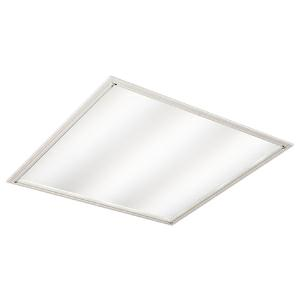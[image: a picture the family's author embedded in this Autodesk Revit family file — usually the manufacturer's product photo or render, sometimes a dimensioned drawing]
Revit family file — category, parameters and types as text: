
# Revit family: 3f_filippi_-_l_320_lgs_3f_filippi_-_21581_-_l_324x10w_led_lgs_596x596
name_source: partatom
category: Lighting Fixtures
units: mm (PartAtom-declared; Revit-internal decimal feet)

## family parameters
Cut with Voids When Loaded = No
Host = Face
Light Source = No
Part Type = Normal
Room Calculation Point = No
Round Connector Dimension = Use Diameter
Shared = No

## types (1)
- 3F Filippi - L 320 LGS (1 x LED, 4292 lm, 45 W, 4000 K)
    Apparent Load = 45 VA
    Approval mark = ENEC
    CIE Flux Codes = 62 88 97 100 100
    Color Rendering = 80
    Color Temperature = 4000 K
    Control Gear = Electronic ballast
    Default Elevation = 1800 mm
    Description = ILLUMINOTECHNICAL
Luminous efficiency 100% (DLOR 100%, ULOR 0%).
Initial luminous flux of the luminaire 4292 lm.
Direct symmetric distribution.
Installation Interdistance Transv.D = 1.16 x hu - Long.D = 1.16 x hu.
Average luminance <3000 cd/m² for radial angles >65°.
Tabular UGR (CIE 117 - 4H-8H; S=0.25H; 70/50/20): RUG 18.8 - 18.8.
Beam angle: 85° - 84°.
Luminous efficacy 95 lm/W.
Lifetime (L93/B10): 30000 h. (tq+25°C)
Lifetime (L90/B10): 50000 h. (tq+25°C)
Lifetime (L85/B10): 80000 h. (tq+25°C)
Lifetime (L80/B10): 100000 h. (tq+25°C)
Sudden decreased luminous flux after 50000 hours: 0% (C0).
Photobiological safety in compliance with IEC/TR 62778: RG0 risk exempt, (IEC 62471).
In compliance with IEC/EN 62722-2-1 - IEC/EN 62717 standards.

SOURCE
4 linear LED modules 10W/840.
Energy efficiency class (UE 2019/2020 - UE 2019/2015): D.
CIE 13.3 Colour rendering index: CRI >80 (R9 <50%).
IES TM-30 Fidelity Index: Rf = 84 Rg = 95.
CCT nominal colour temperature 4000 K.
Colour initial tolerance (MacAdam): SDCM 2.

MECHANICAL
Housing in hot-galvanised steel, painted in white polyester.
Micro-prismatic flat diffuser in transparent methacrylate (PMMA), multilenticular exterior, anti-glare, locked to the white painted aluminium perimetral frame, sealing gasket, hinged opening.
Anti-glare opal polycarbonate filter for brightness uniformity.
Luminaire with limited surface temperature. - D - (EN 60598-2-24)
Dimensions: 596x596 mm, height 80 mm. Weight 4.715 kg.
IP54 protection degree for exposed part, IP20 for recessed part.
Mechanical strength to impacts IK06 (1 joule).
Glow-wire test resistance 650°C.

ELECTRICAL
Halogen Free electronic wiring 230V-50/60Hz, power factor 0.95, THD <25%, constant output current, SELV, class I, 1 driver.
Power of the luminaire 45 W.
CE - IEC 60598-1 - EN 60598-1.
SAFE FLICKER: PstLM=<1 and SVM=<0.4 (IEC TR 61547-1 and IEC TR 63158), to ensure a more comfortable and safe light.
Luminaire compliant with EN 60598-2-22 for power supply from a centralised emergency system CPSS (Central Power Supply System), not incorporated in the luminaire - high risk areas excluded. The default power and flux are 100% in AC and 100% in DC.
Ambient temperature from 0°C to +25°C.
Temperature class T6 max 85°C.
Relative humidity UR: <85%.

INSTALLATION
Lay-in recessed fitting.
On request: pull-up recessed fitting with brackets.
False ceiling carving: 580x580 mm.
All accessories dedicated to this product are available on the Catalog and on our website www.3F-Filippi.com.

APPLICATIONS
Environments: sterilized, aseptic.
In environments with VDU's, managerial offices and staterooms, environments involving accurate visual tasks where a diffused and soft light for an optimum visual comfort and the source total shielding are required.

WARNING
Luminaire designed for disposal/recycling at end-of-life.
Replaceable (LED only) light source by a professional. Replaceable control gear by a professional.
    Height = 0 mm  [stored 0 ft]
    Lamp = 1 x LED
    Lamp Light Flux = 4292 lm
    Lamp Power = 45 W
    Lamp count = 1
    Length = 596 mm
    Lifetime = 50000 h
    Luminous efficacy = 95 lm/W
    Manufacturer = 3F Filippi
    ModVariant = No
    Model = 3F Filippi - 21581 - L 324x10W LED LGS 596x596
    Mounting Place = Ceiling
    Mounting Type = Recessed
    Number of Poles = 1
    OnlyDefault = Yes
    Power Factor = 1
    Product Name = 3F Filippi - L 320 LGS
    Product group = recessed luminaire
    ProductGroupID = 4
    Protection Class = Protection class I
    Protection Degree = IP 20
    RLX_Detail_Level = 1
    RLX_Emergency_Light_Flux = 0 lm
    RLX_Emergency_Type = 0
    RLX_Emergency_Type_DB = No
    RlxData = <blob elided: 34057 chars, md5=329d846d>
    Socket = socket
    Standby Power = 0 W
    System Light Flux = 4292 lm
    System Power = 45 W
    Type Comments = Product without accessories
    Type Image = 3ffilippi_l_320_led_lgs.jpg
    URL = http://relux.com
    VarID = ---
    Voltage = 0 V
    Weight = 0.00 kg
    Width = 596 mm

note: [stored X ft] marks values corroborated as IEEE doubles in the binary element streams (Revit-internal decimal feet)

## geometry (parser evidence)
native form markers: Blend x4, Sweep x9
no freeform markers — native parametric forms only
